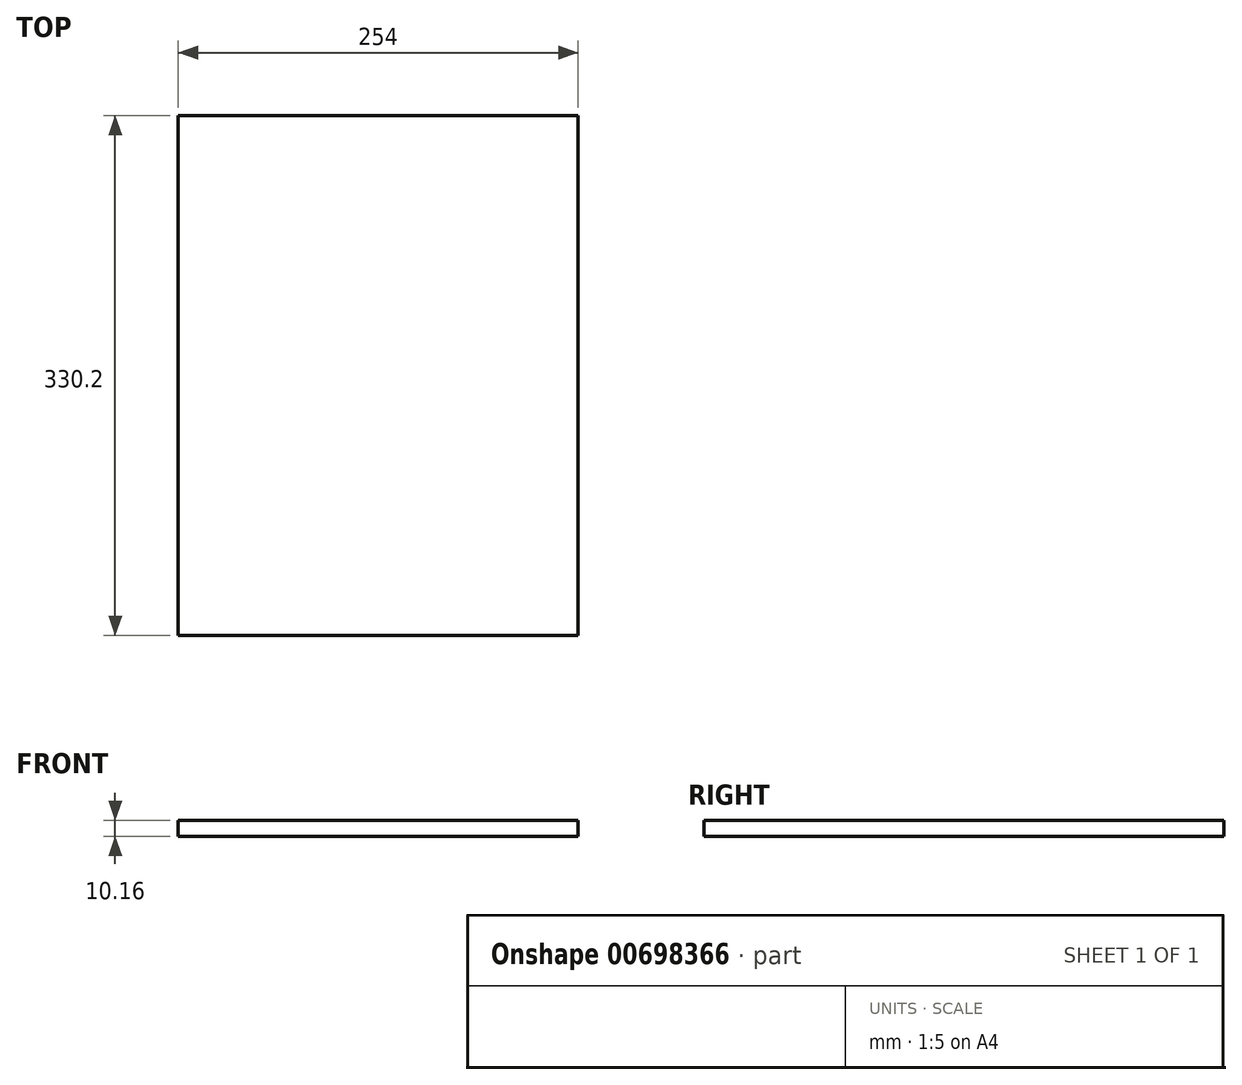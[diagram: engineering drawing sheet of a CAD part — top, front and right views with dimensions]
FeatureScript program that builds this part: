
annotation { "Feature Type Name" : "Feature", "Feature Type Description" : "" }
export const myFeature = defineFeature(function(context is Context, id is Id, definition is map)
    precondition{}
    {
        {
            var Q0;
            Q0=qCreatedBy(makeId("Front.planeOp"),FACE);
            var sketch = newSketch(context, id + "F0", { "sketchPlane" : qUnion([Q0])});
            skLineSegment(sketch, "E0.bottom", {"start": v(-127, 5.08) * mm, "end": v(127, 5.08) * mm});
            skLineSegment(sketch, "E0.top", {"start": v(-127, -5.08) * mm, "end": v(127, -5.08) * mm});
            skLineSegment(sketch, "E0.left", {"start": v(-127, 5.08) * mm, "end": v(-127, -5.08) * mm});
            skLineSegment(sketch, "E0.right", {"start": v(127, 5.08) * mm, "end": v(127, -5.08) * mm});
            skPoint(sketch, "E0.middle", {"position": v(0, 0) * mm});
            skSolve(sketch);
        }
        {
            var Q0;
            Q0=makeQuery(id+"F0.imprint","IMPRINT",FACE,{"disambiguationData":[TD([[makeQuery(id+"F0.imprint","IMPRINT",EDGE,{"derivedFrom":sQuery(id+"F0.wireOp",EDGE,"E0.bottom")}),-1.0]])]});
            extrude(context, id + "F1", {"entities" : qUnion([Q0]), "depth" : 330.2 * mm, "offsetDistance" : 25.4 * mm});
        }
    });
